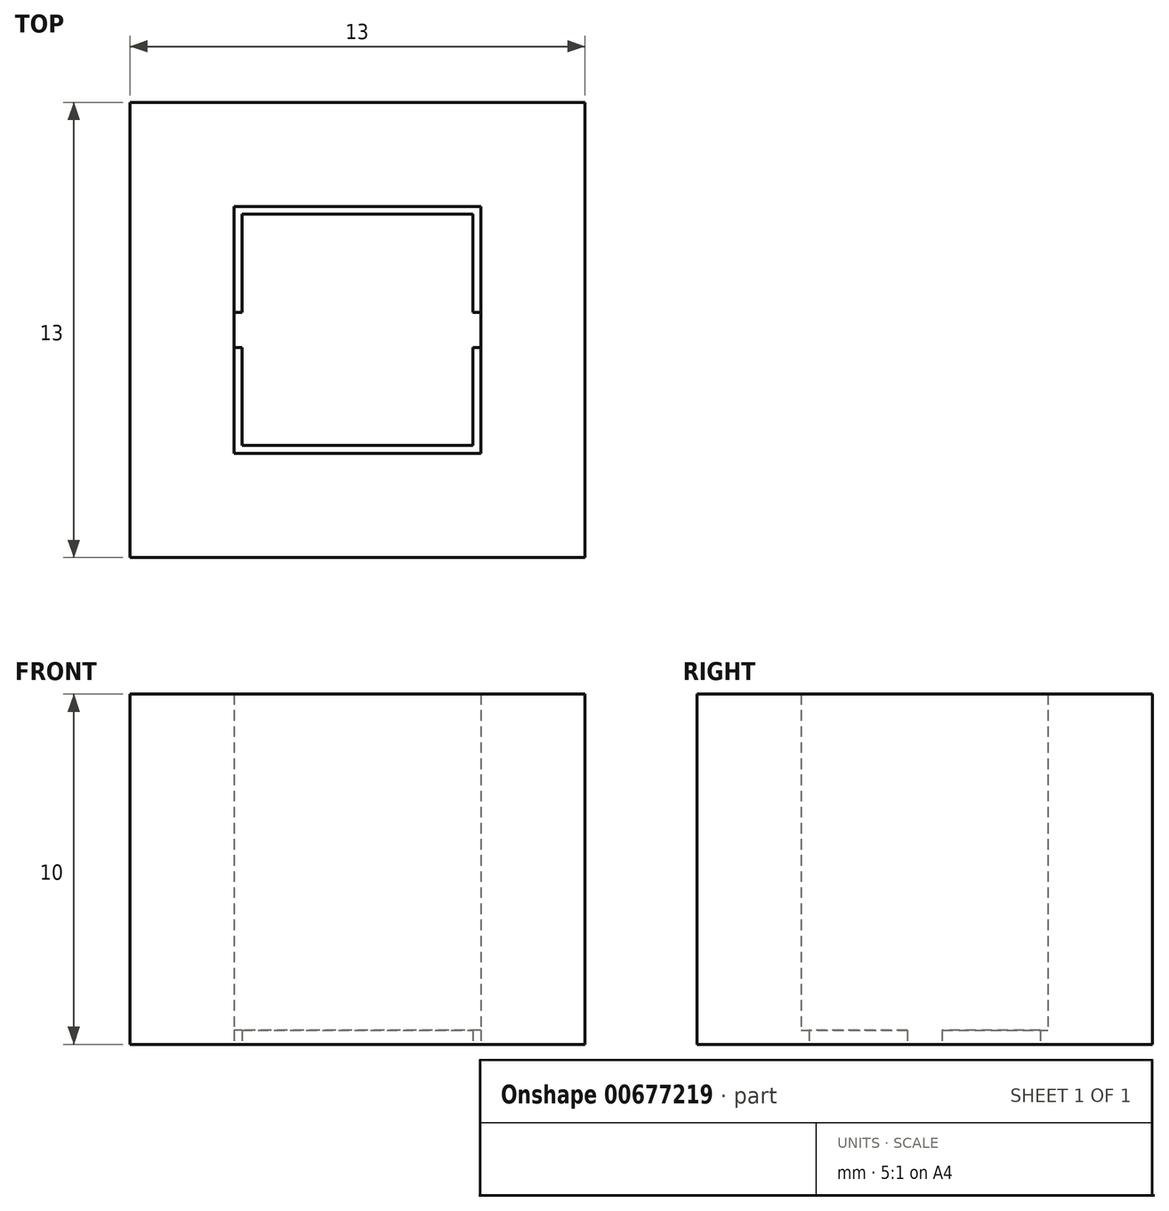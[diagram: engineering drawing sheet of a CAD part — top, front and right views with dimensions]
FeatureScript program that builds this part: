
annotation { "Feature Type Name" : "Feature", "Feature Type Description" : "" }
export const myFeature = defineFeature(function(context is Context, id is Id, definition is map)
    precondition{}
    {
        {
            var Q0;
            Q0=qCreatedBy(makeId("Top.planeOp"),FACE);
            var sketch = newSketch(context, id + "F0", { "sketchPlane" : qUnion([Q0])});
            skLineSegment(sketch, "E0.bottom", {"start": v(-6.6, 6.6) * mm, "end": v(0, 6.6) * mm});
            skLineSegment(sketch, "E0.top", {"start": v(-6.6, 0) * mm, "end": v(0, 0) * mm});
            skLineSegment(sketch, "E0.left", {"start": v(-6.6, 6.6) * mm, "end": v(-6.6, 0) * mm});
            skLineSegment(sketch, "E0.right", {"start": v(0, 6.6) * mm, "end": v(0, 0) * mm});
            skLineSegment(sketch, "E1.bottom", {"start": v(0.22, -0.23) * mm, "end": v(-6.83, -0.23) * mm});
            skLineSegment(sketch, "E1.top", {"start": v(0.23, 6.82) * mm, "end": v(-6.83, 6.82) * mm});
            skLineSegment(sketch, "E1.left", {"start": v(0.22, -0.23) * mm, "end": v(0.23, 6.83) * mm});
            skLineSegment(sketch, "E1.right", {"start": v(-6.83, -0.23) * mm, "end": v(-6.82, 6.83) * mm});
            skPoint(sketch, "E1.middle", {"position": v(-3.3, 3.3) * mm});
            skPoint(sketch, "E1.middle.positionSnap0", {"position": v(0, 3.3) * mm});
            skPoint(sketch, "E1.middle.positionSnap1", {"position": v(-3.3, 6.6) * mm});
            skPoint(sketch, "E1.centerSnap0", {"position": v(0, 3.3) * mm});
            skPoint(sketch, "E1.centerSnap1", {"position": v(-3.3, 6.6) * mm});
            skLineSegment(sketch, "E2.bottom", {"start": v(0.23, 2.8) * mm, "end": v(-6.83, 2.8) * mm});
            skLineSegment(sketch, "E2.top", {"start": v(0.23, 3.8) * mm, "end": v(-6.83, 3.8) * mm});
            skLineSegment(sketch, "E2.left", {"start": v(0.22, 2.8) * mm, "end": v(0.22, 3.8) * mm});
            skLineSegment(sketch, "E2.right", {"start": v(-6.82, 2.8) * mm, "end": v(-6.82, 3.8) * mm});
            skLineSegment(sketch, "E3.bottom", {"start": v(-9.8, -3.2) * mm, "end": v(3.2, -3.2) * mm});
            skLineSegment(sketch, "E3.top", {"start": v(-9.8, 9.8) * mm, "end": v(3.2, 9.8) * mm});
            skLineSegment(sketch, "E3.left", {"start": v(-9.8, -3.2) * mm, "end": v(-9.8, 9.8) * mm});
            skLineSegment(sketch, "E3.right", {"start": v(3.2, -3.2) * mm, "end": v(3.2, 9.8) * mm});
            skSolve(sketch);
        }
        {
            var Q0;
            {var subQ5=sQuery(id+"F0.wireOp",EDGE,"E2.left");Q0=makeQuery(id+"F0.imprint","IMPRINT",FACE,{"disambiguationData":[TD([[makeQuery(id+"F0.imprint","IMPRINT",EDGE,{"derivedFrom":subQ5}),1.0]])]});}
            var Q1;
            {var subQ4=sQuery(id+"F0.wireOp",EDGE,"E1.bottom");Q1=makeQuery(id+"F0.imprint","IMPRINT",FACE,{"disambiguationData":[TD([[makeQuery(id+"F0.imprint","IMPRINT",EDGE,{"derivedFrom":subQ4}),1.0]])]});}
            var Q2;
            {var subQ5=sQuery(id+"F0.wireOp",EDGE,"E2.right");Q2=makeQuery(id+"F0.imprint","IMPRINT",FACE,{"disambiguationData":[TD([[makeQuery(id+"F0.imprint","IMPRINT",EDGE,{"derivedFrom":subQ5}),-1.0]])]});}
            extrude(context, id + "F1", {"entities" : qUnion([Q0, Q1, Q2]), "depth" : 10 * mm, "offsetDistance" : 25 * mm});
        }
        {
            var Q0;
            {var subQ2=sQuery(id+"F0.wireOp",EDGE,"E0.top");Q0=makeQuery(id+"F0.imprint","IMPRINT",FACE,{"disambiguationData":[TD([[makeQuery(id+"F0.imprint","IMPRINT",EDGE,{"derivedFrom":subQ2}),-1.0]])]});}
            var Q1;
            {var subQ2=sQuery(id+"F0.wireOp",EDGE,"E0.bottom");Q1=makeQuery(id+"F0.imprint","IMPRINT",FACE,{"disambiguationData":[TD([[makeQuery(id+"F0.imprint","IMPRINT",EDGE,{"derivedFrom":subQ2}),1.0]])]});}
            extrude(context, id + "F2", {"entities" : qUnion([Q0, Q1]), "operationType" : NewBodyOperationType.ADD, "depth" : 0.4 * mm, "offsetDistance" : 25 * mm});
        }
        {
            var Q0;
            Q0=makeQuery(id+"F1.opExtrude","SWEPT_FACE",FACE,{"disambiguationData":[OSD([sQuery(id+"F0.wireOp",EDGE,"E3.right")])]});
            var sketch = newSketch(context, id + "F3", { "sketchPlane" : qUnion([Q0])});
            skLineSegment(sketch, "E4", {"start": v(9.8, 0) * mm, "end": v(-3.2, 0) * mm});
            skLineSegment(sketch, "E5", {"start": v(9.8, 0) * mm, "end": v(9.8, 3.5) * mm});
            skLineSegment(sketch, "E6", {"start": v(9.8, 3.5) * mm, "end": v(-3.2, 3.5) * mm});
            skLineSegment(sketch, "E7", {"start": v(-3.2, 3.5) * mm, "end": v(-3.2, 0) * mm});
            skSolve(sketch);
        }
    });
